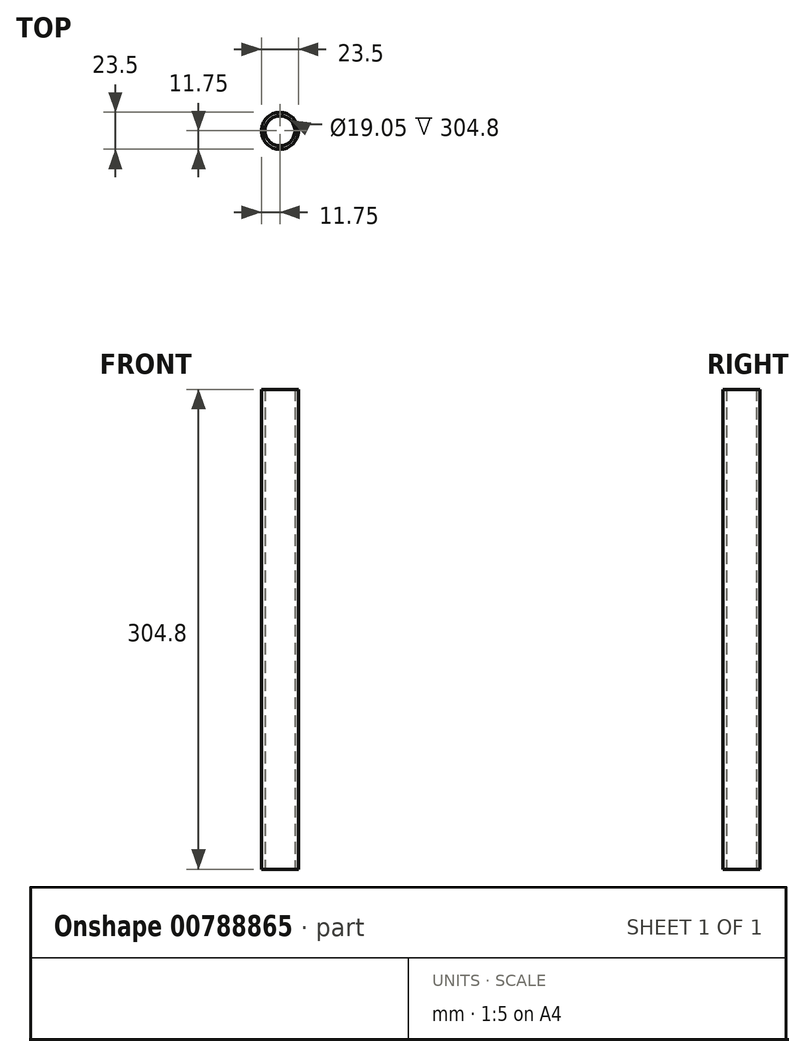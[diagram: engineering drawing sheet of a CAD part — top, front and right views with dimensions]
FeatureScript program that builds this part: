
annotation { "Feature Type Name" : "Feature", "Feature Type Description" : "" }
export const myFeature = defineFeature(function(context is Context, id is Id, definition is map)
    precondition{}
    {
        {
            var Q0;
            Q0=qCreatedBy(makeId("Top.planeOp"),FACE);
            var sketch = newSketch(context, id + "F0", { "sketchPlane" : qUnion([Q0])});
            skCircle(sketch, "E0", {"center": v(0, 0) * mm, "radius": 9.53 * mm});
            skCircle(sketch, "E1", {"center": v(0, 0) * mm, "radius": 11.75 * mm});
            skSolve(sketch);
        }
        {
            var Q0;
            Q0 = qSketchRegion(id + "F0", true);
            extrude(context, id + "F1", {"entities" : qUnion([Q0]), "depth" : (25.4 * 12) * mm, "offsetDistance" : 25 * mm});
        }
    });
